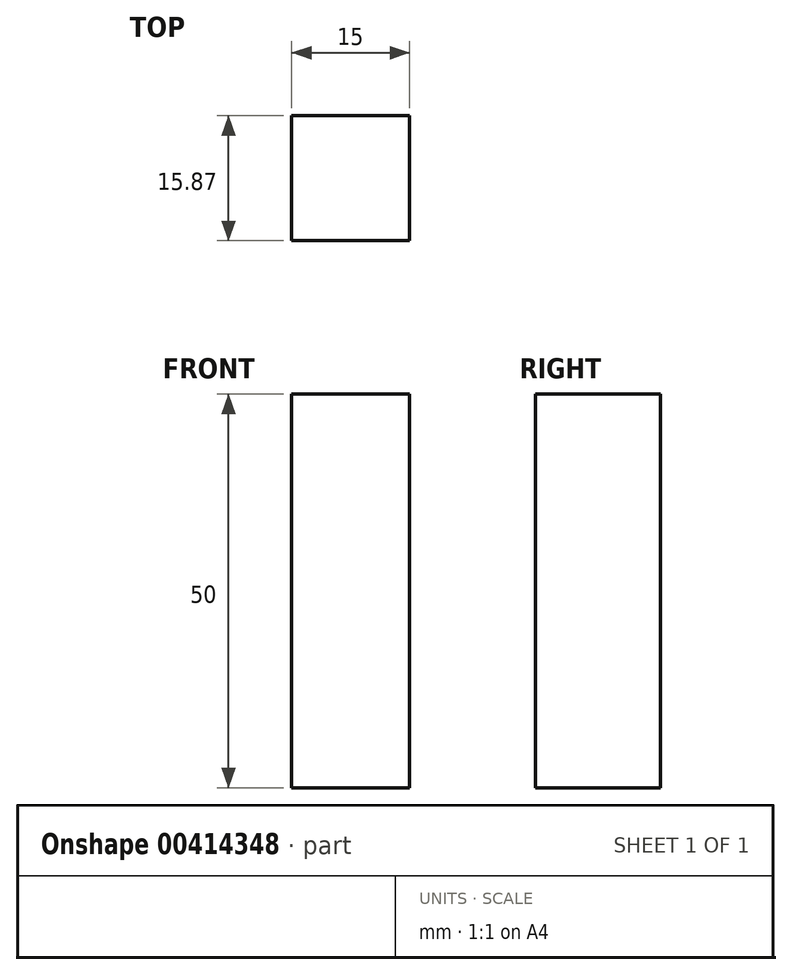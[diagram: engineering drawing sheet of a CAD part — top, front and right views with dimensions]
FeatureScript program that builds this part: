
annotation { "Feature Type Name" : "Feature", "Feature Type Description" : "" }
export const myFeature = defineFeature(function(context is Context, id is Id, definition is map)
    precondition{}
    {
        {
            var Q0;
            Q0=qCreatedBy(makeId("Top.planeOp"),FACE);
            var sketch = newSketch(context, id + "F0", { "sketchPlane" : qUnion([Q0])});
            skLineSegment(sketch, "E0.bottom", {"start": v(-21.06, 15.87) * mm, "end": v(-6.06, 15.87) * mm});
            skLineSegment(sketch, "E0.top", {"start": v(-21.06, 0) * mm, "end": v(-6.06, 0) * mm});
            skLineSegment(sketch, "E0.left", {"start": v(-21.06, 15.87) * mm, "end": v(-21.06, 0) * mm});
            skLineSegment(sketch, "E0.right", {"start": v(-6.06, 15.87) * mm, "end": v(-6.06, 0) * mm});
            skSolve(sketch);
        }
        {
            var Q0;
            Q0=makeQuery(id+"F0.imprint","IMPRINT",FACE,{"disambiguationData":[TD([[makeQuery(id+"F0.imprint","IMPRINT",EDGE,{"derivedFrom":sQuery(id+"F0.wireOp",EDGE,"E0.bottom")}),-1.0]])]});
            extrude(context, id + "F1", {"entities" : qUnion([Q0]), "depth" : 50 * mm});
        }
    });
